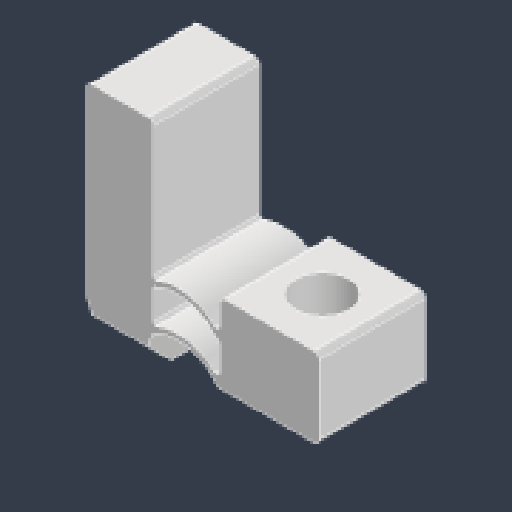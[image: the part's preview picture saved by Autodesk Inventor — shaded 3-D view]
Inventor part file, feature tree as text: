
AUTODESK INVENTOR PART (.ipt)
format: ipt  version: 2023.4 (Build 274418000, 418)  size: 220,672 bytes
history: native  units: mm
features: sketch x3, extrude x2, chamfer x2, fillet x2, hole x1
ambient origin geometry x8: Origin, YZ Plane, XZ Plane, XY Plane, X Axis, Y Axis, Z Axis, Center Point
bodies: Solid1 (feature_tree)
feature tree (10):
  extrude  "Extrusion1"  Depth=18.0mm
  chamfer  "Chamfer1"  Distance=3.0mm
  chamfer  "Chamfer2"  Distance=5.0mm
  fillet  "Fillet1"  Radius=9.0mm
  fillet  "Fillet2"  Radius=3.0mm
  hole  "Hole2"  [1 undecoded]
  extrude  "Extrusion2"  Depth=8.0mm
  sketch  "Sketch1"  dims[d0=5.0mm d1=18.0mm]
  sketch  "Sketch3"  dims[d2=30.0mm]
  sketch  "Sketch4"  dims[d3=3.0mm d4=3.0mm d5=5.0mm d8=9.0mm d9=3.0mm d10=2.0mm d11=3.490659mm d12=0.4mm d13=4.0mm d14=3.0mm d15=8.0mm d16=0.0mm d25=3.0mm d26=2.0mm d27=45.0deg d28=3.0mm d29=2.0mm d30=45.0deg d31=0.2mm d32=0.4mm d34=4.0mm d35=6.0mm d36=4.0mm d37=2.0mm d38=90.0deg d39=8.0mm d40=20.594885mm d41=0.0mm d42=0.0mm]
note: 1 required parameter value undecoded (feature->parameter linkage not recoverable at this tier; creation-order binding heuristic only, values carry confidence <= 0.55)
